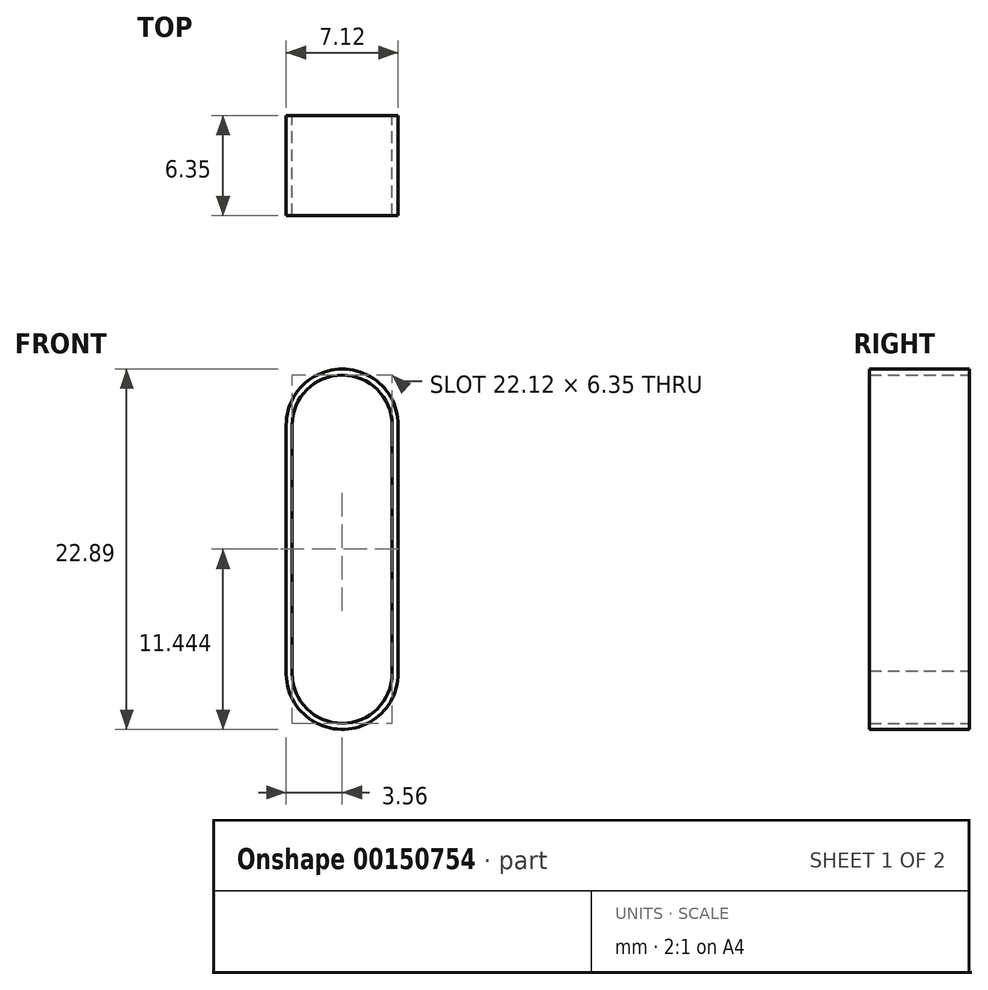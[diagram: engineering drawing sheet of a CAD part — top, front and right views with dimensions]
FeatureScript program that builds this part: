
annotation { "Feature Type Name" : "Feature", "Feature Type Description" : "" }
export const myFeature = defineFeature(function(context is Context, id is Id, definition is map)
    precondition{}
    {
        {
            var Q0;
            Q0=qCreatedBy(makeId("Front.planeOp"),FACE);
            var sketch = newSketch(context, id + "F0", { "sketchPlane" : qUnion([Q0])});
            skArc(sketch, "E0", {"start": v(3.18, 0) * mm, "mid": v(0, 3.18) * mm, "end": v(-3.18, 0) * mm});
            skArc(sketch, "E1", {"start": v(-3.18, -15.77) * mm, "mid": v(0, -18.95) * mm, "end": v(3.18, -15.77) * mm});
            skArc(sketch, "E2", {"start": v(3.56, 0) * mm, "mid": v(0, 3.56) * mm, "end": v(-3.56, 0) * mm});
            skArc(sketch, "E3", {"start": v(-3.55, -15.61) * mm, "mid": v(-0.08, -19.33) * mm, "end": v(3.56, -15.77) * mm});
            skLineSegment(sketch, "E4", {"start": v(-3.56, 0) * mm, "end": v(-3.55, -15.61) * mm});
            skLineSegment(sketch, "E5", {"start": v(-3.17, -15.77) * mm, "end": v(-3.18, 0) * mm});
            skLineSegment(sketch, "E6", {"start": v(3.17, -15.77) * mm, "end": v(3.18, 0) * mm});
            skLineSegment(sketch, "E7", {"start": v(3.56, -15.77) * mm, "end": v(3.56, 0) * mm});
            skSolve(sketch);
        }
        {
            var Q0;
            Q0=makeQuery(id+"F0.imprint","IMPRINT",FACE,{"disambiguationData":[TD([[makeQuery(id+"F0.imprint","IMPRINT",EDGE,{"derivedFrom":sQuery(id+"F0.wireOp",EDGE,"E0")}),-1.0]])]});
            extrude(context, id + "F1", {"entities" : qUnion([Q0]), "depth" : 6.35 * mm});
        }
    });
